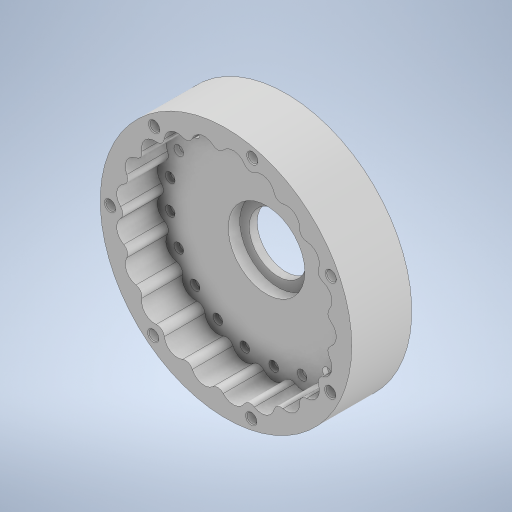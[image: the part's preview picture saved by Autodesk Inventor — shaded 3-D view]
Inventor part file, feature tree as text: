
AUTODESK INVENTOR PART (.ipt)
format: ipt  version: 2023 (Build 270158000, 158)  size: 439,296 bytes
history: native  units: in
note: dims shown in document units (in); Inventor stores cm internally (conversion verified against a paired STEP export)
features: sketch x5, extrude x3, hole x2, pattern_circular x2, reference x2, other x2
ambient origin geometry x8: Origin, YZ Plane, XZ Plane, XY Plane, X Axis, Y Axis, Z Axis, Center Point
bodies: Solid1 (feature_tree)
feature tree (16):
  extrude  "Extrusion1"  Depth=0.0591in
  extrude  "Extrusion2"  Depth=2.6772in TaperAngle=360.0deg
  hole  "Hole1"  [1 undecoded]
  extrude  "Extrusion4"  Depth=0.2362in
  pattern_circular  "Circular Pattern1"  Count=21 Angle=360.0deg
  hole  "Hole2"  [1 undecoded]
  pattern_circular  "Circular Pattern2"  [2 undecoded]
  sketch  "Sketch2"  dims[d0=6.1024in d3=0.0591in]
  reference  "Reference1"
  reference  "Reference2"
  sketch  "Sketch3"  dims[d4=2.6772in d5=8.2677in d7=360.0deg]
  sketch  "Sketch5"  dims[d9=0.9843in d10=0.0in d11=0.4724in d12=0.0in]
  sketch  "Sketch6"  dims[d16=1.4in d17=0.2362in d18=1.86in d19=0.28in d20=90.0deg d21=0.315in d22=0.8108in d23=0.2362in]
  sketch  "Sketch7"  dims[d24=0.1181in d25=0.0in d26=8.2677in d27=360.0deg d29=0.2362in d30=0.2362in d31=0.2756in d32=0.3937in d33=90.0deg d34=0.2362in d35=0.0in d36=2.7559in d37=360.0deg d39=5.6299in]
  other  "Assembly1"
  other  "Bearings:1"
note: 4 required parameter values undecoded (feature->parameter linkage not recoverable at this tier; creation-order binding heuristic only, values carry confidence <= 0.55)
